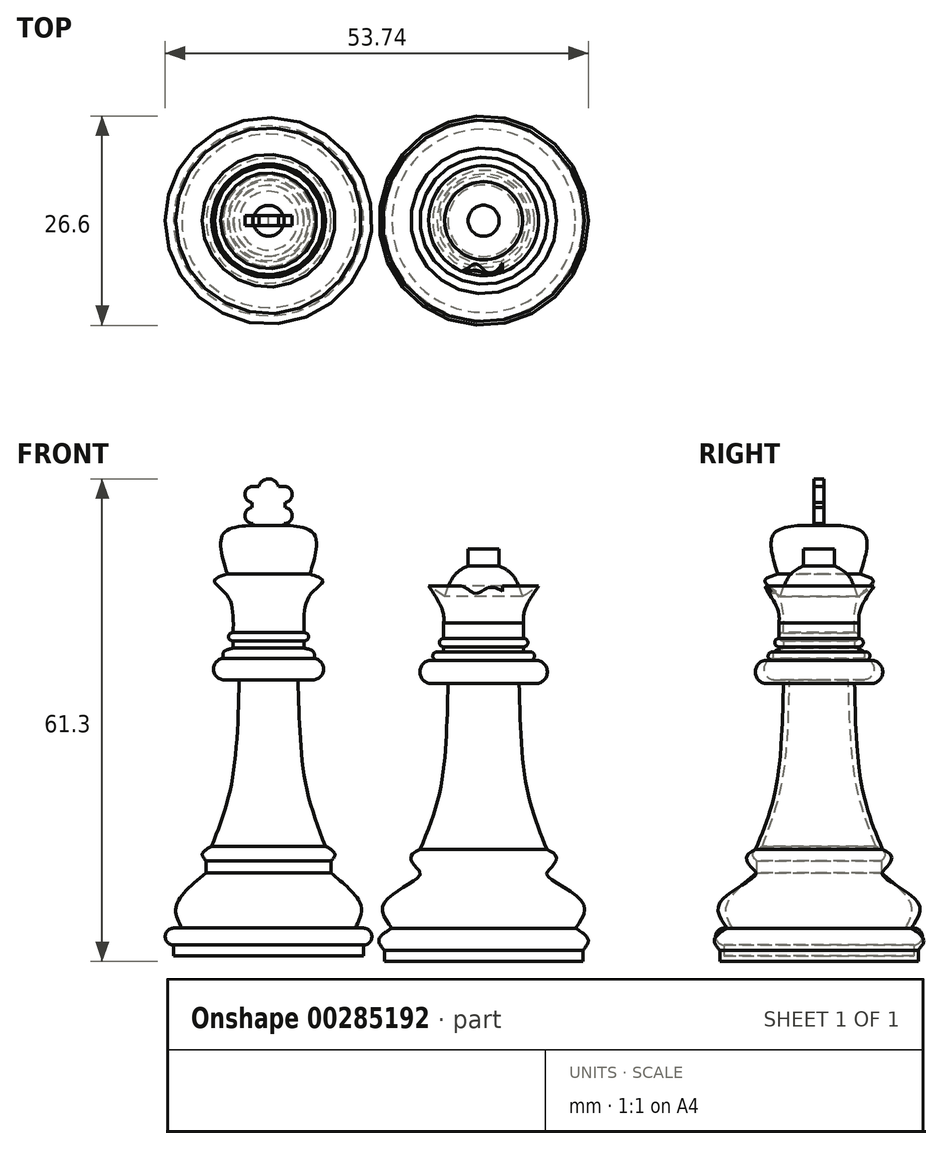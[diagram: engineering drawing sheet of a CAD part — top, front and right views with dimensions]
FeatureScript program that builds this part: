
annotation { "Feature Type Name" : "Feature", "Feature Type Description" : "" }
export const myFeature = defineFeature(function(context is Context, id is Id, definition is map)
    precondition{}
    {
        {
            var Q0;
            Q0=qCreatedBy(makeId("Front.planeOp"),FACE);
            var sketch = newSketch(context, id + "F0", { "sketchPlane" : qUnion([Q0])});
            skLineSegment(sketch, "E0", {"start": v(14.8, -63.72) * mm, "end": v(26.85, -63.72) * mm});
            skLineSegment(sketch, "E1", {"start": v(14.8, -63.72) * mm, "end": v(14.8, -9) * mm});
            skPoint(sketch, "E2.orphan", {"position": v(27.5, -63.72) * mm});
            skPoint(sketch, "E3.orphan", {"position": v(2.1, -63.72) * mm});
            skFitSpline(sketch, "E4", {"points": [v(14.8, -9) * mm, v(20.53, -10.08) * mm, v(20.03, -15.2) * mm], "startDerivative": vector(14.26, 0.1) * mm, "endDerivative": vector(-3.97, -12.61) * mm});
            skFitSpline(sketch, "E5", {"points": [v(20.03, -15.2) * mm, v(21.68, -16.07) * mm, v(20.03, -17.92) * mm, v(19.3, -22.65) * mm], "startDerivative": vector(9.24, -2.9) * mm, "endDerivative": vector(0.37, -12.43) * mm});
            skLineSegment(sketch, "E6", {"start": v(19.3, -23.67) * mm, "end": v(19.3, -24.6) * mm});
            skArc(sketch, "E7", {"start": v(19.3, -23.67) * mm, "mid": v(19.88, -23.16) * mm, "end": v(19.3, -22.65) * mm});
            skFitSpline(sketch, "E8", {"points": [v(19.3, -24.6) * mm, v(20.5, -25.09) * mm, v(20.57, -25.91) * mm], "startDerivative": vector(2.7, -0.6) * mm, "endDerivative": vector(-0.28, -2.08) * mm});
            skLineSegment(sketch, "E9", {"start": v(20.57, -25.91) * mm, "end": v(20.57, -28.63) * mm, "construction": true});
            skArc(sketch, "E10", {"start": v(20.57, -28.63) * mm, "mid": v(21.8, -27.27) * mm, "end": v(20.57, -25.91) * mm});
            skLineSegment(sketch, "E11", {"start": v(20.57, -28.63) * mm, "end": v(18.53, -28.63) * mm});
            skFitSpline(sketch, "E12", {"points": [v(18.53, -28.63) * mm, v(19.48, -41.7) * mm, v(22, -49.77) * mm], "startDerivative": vector(0.63, -25.08) * mm, "endDerivative": vector(6.55, -16.9) * mm});
            skFitSpline(sketch, "E13", {"points": [v(22, -49.77) * mm, v(23.22, -50.77) * mm, v(22.72, -51.65) * mm], "startDerivative": vector(3.09, -1.76) * mm, "endDerivative": vector(-1.85, -2.02) * mm});
            skLineSegment(sketch, "E14", {"start": v(22.72, -51.65) * mm, "end": v(22.72, -53.19) * mm});
            skFitSpline(sketch, "E15", {"points": [v(22.72, -53.19) * mm, v(26.53, -57.34) * mm, v(25.81, -60.17) * mm], "startDerivative": vector(8.97, -7.26) * mm, "endDerivative": vector(-3.45, -6.68) * mm});
            skLineSegment(sketch, "E16", {"start": v(25.81, -60.17) * mm, "end": v(26.85, -60.17) * mm});
            skArc(sketch, "E17", {"start": v(26.85, -62.31) * mm, "mid": v(27.92, -61.24) * mm, "end": v(26.85, -60.17) * mm});
            skLineSegment(sketch, "E18", {"start": v(26.85, -62.31) * mm, "end": v(26.85, -63.72) * mm});
            skLineSegment(sketch, "E19.trimOffspring", {"start": v(27.5, -63.72) * mm, "end": v(27.53, -63.72) * mm});
            skLineSegment(sketch, "E20", {"start": v(13.55, -4.06) * mm, "end": v(16.03, -4.06) * mm, "construction": true});
            skLineSegment(sketch, "E21", {"start": v(14.8, -9) * mm, "end": v(14.8, -4.06) * mm, "construction": true});
            skArc(sketch, "E22", {"start": v(16.03, -4.06) * mm, "mid": v(14.8, -3.11) * mm, "end": v(13.55, -4.06) * mm});
            skArc(sketch, "E23", {"start": v(16.9, -6.1) * mm, "mid": v(17.8, -5) * mm, "end": v(16.75, -4.06) * mm});
            skLineSegment(sketch, "E24", {"start": v(16.9, -6.1) * mm, "end": v(16.9, -6.75) * mm});
            skLineSegment(sketch, "E25", {"start": v(16.9, -6.42) * mm, "end": v(15.64, -6.42) * mm, "construction": true});
            skArc(sketch, "E26.MirrorCS", {"start": v(16.9, -6.75) * mm, "mid": v(17.8, -7.84) * mm, "end": v(16.75, -8.78) * mm});
            skLineSegment(sketch, "E27", {"start": v(16.75, -4.06) * mm, "end": v(16.03, -4.06) * mm});
            skLineSegment(sketch, "E28.MirrorCS", {"start": v(12.84, -4.06) * mm, "end": v(13.55, -4.06) * mm});
            skArc(sketch, "E29.MirrorCS", {"start": v(12.68, -6.1) * mm, "mid": v(11.8, -5) * mm, "end": v(12.84, -4.06) * mm});
            skLineSegment(sketch, "E30.MirrorCS", {"start": v(12.68, -6.1) * mm, "end": v(12.68, -6.75) * mm});
            skArc(sketch, "E31.MirrorCS", {"start": v(12.68, -6.75) * mm, "mid": v(11.8, -7.84) * mm, "end": v(12.84, -8.78) * mm});
            skLineSegment(sketch, "E32", {"start": v(16.75, -8.78) * mm, "end": v(16.75, -9.01) * mm});
            skLineSegment(sketch, "E33.MirrorCS", {"start": v(12.84, -8.78) * mm, "end": v(12.84, -9.01) * mm});
            skLineSegment(sketch, "E34", {"start": v(12.84, -9.01) * mm, "end": v(16.75, -9.01) * mm});
            skLineSegment(sketch, "E35", {"start": v(42.1, -10.26) * mm, "end": v(42.1, -68.9) * mm, "construction": true});
            skLineSegment(sketch, "E36", {"start": v(42.1, -12) * mm, "end": v(44.07, -12) * mm});
            skLineSegment(sketch, "E37", {"start": v(44.07, -12) * mm, "end": v(44.07, -14.15) * mm});
            skFitSpline(sketch, "E38", {"points": [v(44.07, -14.15) * mm, v(45.72, -15.25) * mm, v(47.05, -18.05) * mm], "startDerivative": vector(4.01, -1.9) * mm, "endDerivative": vector(2.02, -5.76) * mm});
            skLineSegment(sketch, "E39", {"start": v(47.05, -18.05) * mm, "end": v(49.09, -16.7) * mm});
            skFitSpline(sketch, "E40", {"points": [v(49.09, -16.7) * mm, v(47.3, -19.84) * mm, v(47.18, -21.43) * mm], "startDerivative": vector(-3.76, -5.6) * mm, "endDerivative": vector(0.22, -3.72) * mm});
            skLineSegment(sketch, "E41", {"start": v(42.1, -21.43) * mm, "end": v(42.1, -12) * mm});
            skLineSegment(sketch, "E42", {"start": v(47.18, -23.37) * mm, "end": v(47.18, -21.43) * mm});
            skArc(sketch, "E43", {"start": v(47.18, -24.44) * mm, "mid": v(47.73, -23.9) * mm, "end": v(47.18, -23.37) * mm});
            skLineSegment(sketch, "E44", {"start": v(47.18, -24.44) * mm, "end": v(47.18, -25.07) * mm});
            skLineSegment(sketch, "E45", {"start": v(47.18, -25.07) * mm, "end": v(48.02, -25.07) * mm});
            skArc(sketch, "E46", {"start": v(48.02, -26.17) * mm, "mid": v(48.57, -25.62) * mm, "end": v(48.02, -25.07) * mm});
            skLineSegment(sketch, "E47", {"start": v(48.02, -26.17) * mm, "end": v(49.07, -26.17) * mm});
            skArc(sketch, "E48", {"start": v(49.07, -29.08) * mm, "mid": v(50.2, -27.62) * mm, "end": v(49.07, -26.17) * mm});
            skLineSegment(sketch, "E49", {"start": v(49.07, -29.08) * mm, "end": v(46.63, -29.08) * mm});
            skFitSpline(sketch, "E50", {"points": [v(46.63, -29.08) * mm, v(47.57, -42.31) * mm, v(50.16, -50.2) * mm], "startDerivative": vector(0.52, -25.34) * mm, "endDerivative": vector(6.78, -16.56) * mm});
            skFitSpline(sketch, "E51", {"points": [v(50.16, -50.2) * mm, v(51.35, -51.1) * mm, v(50.65, -52.5) * mm, v(50.16, -53.43) * mm, v(54.72, -56.97) * mm, v(53.76, -60.18) * mm], "startDerivative": vector(10.4, -4.81) * mm, "endDerivative": vector(-10.06, -13.62) * mm});
            skFitSpline(sketch, "E52", {"points": [v(53.76, -60.18) * mm, v(55.4, -61.66) * mm, v(54.71, -62.98) * mm], "startDerivative": vector(4.21, -2.63) * mm, "endDerivative": vector(-2.54, -2.98) * mm});
            skLineSegment(sketch, "E53", {"start": v(54.71, -62.98) * mm, "end": v(54.71, -64.41) * mm});
            skLineSegment(sketch, "E54", {"start": v(54.71, -64.41) * mm, "end": v(42.1, -64.41) * mm});
            skLineSegment(sketch, "E55", {"start": v(42.1, -64.41) * mm, "end": v(42.1, -21.43) * mm});
            skSolve(sketch);
        }
        {
            var Q0;
            Q0=makeQuery(id+"F0.imprint","IMPRINT",FACE,{"disambiguationData":[TD([[makeQuery(id+"F0.imprint","IMPRINT",EDGE,{"derivedFrom":sQuery(id+"F0.wireOp",EDGE,"E0")}),1.0]])]});
            var Q1;
            Q1=sQuery(id+"F0.wireOp",EDGE,"E1");
            revolve(context, id + "F1", {"entities" : qUnion([Q0]), "axis" : qUnion([Q1]), "revolveType" : RevolveType.FULL});
        }
        {
            var Q0;
            Q0=makeQuery(id+"F0.imprint","IMPRINT",FACE,{"disambiguationData":[TD([[makeQuery(id+"F0.imprint","IMPRINT",EDGE,{"derivedFrom":sQuery(id+"F0.wireOp",EDGE,"E22")}),1.0]])]});
            extrude(context, id + "F2", {"entities" : qUnion([Q0]), "endBound" : BoundingType.SYMMETRIC, "depth" : 1.27 * mm});
        }
        {
            var Q0;
            Q0=makeQuery(id+"F0.imprint","IMPRINT",FACE,{"disambiguationData":[TD([[makeQuery(id+"F0.imprint","IMPRINT",EDGE,{"derivedFrom":sQuery(id+"F0.wireOp",EDGE,"E36")}),-1.0]])]});
            var Q1;
            Q1=sQuery(id+"F0.wireOp",EDGE,"E35");
            revolve(context, id + "F3", {"entities" : qUnion([Q0]), "axis" : qUnion([Q1]), "revolveType" : RevolveType.FULL});
        }
        {
            var Q0;
            Q0=qCreatedBy(makeId("Front.planeOp"),FACE);
            var sketch = newSketch(context, id + "F4", { "sketchPlane" : qUnion([Q0])});
            skFitSpline(sketch, "E56", {"points": [v(38.82, -16.54) * mm, v(40.08, -17.1) * mm, v(41.26, -17.64) * mm, v(42.64, -16.93) * mm, v(43.93, -17.08) * mm, v(44.49, -17.41) * mm], "startDerivative": vector(5.96, -2.19) * mm, "endDerivative": vector(3.3, -2.3) * mm});
            skLineSegment(sketch, "E57", {"start": v(44.49, -17.41) * mm, "end": v(44.49, -16.54) * mm});
            skLineSegment(sketch, "E58", {"start": v(44.49, -16.54) * mm, "end": v(38.82, -16.54) * mm});
            skSolve(sketch);
        }
        {
            var Q0;
            Q0=makeQuery(id+"F4.imprint","IMPRINT",FACE,{"disambiguationData":[TD([[makeQuery(id+"F4.imprint","IMPRINT",EDGE,{"derivedFrom":sQuery(id+"F4.wireOp",EDGE,"E56")}),1.0]])]});
            extrude(context, id + "F5", {"entities" : qUnion([Q0]), "operationType" : NewBodyOperationType.REMOVE, "depth" : 13.82 * mm, "hasSecondDirection" : true, "secondDirectionOppositeDirection" : false, "secondDirectionDepth" : 4.78 * mm});
        }
    });
